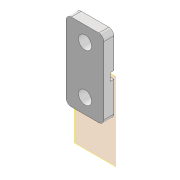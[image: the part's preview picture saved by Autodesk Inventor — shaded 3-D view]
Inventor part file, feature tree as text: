
AUTODESK INVENTOR PART (.ipt)
format: ipt  version: 2020 (Build 240168000, 168)  size: 113,664 bytes
history: native  units: mm
features: other x5, extrude x2, fillet x2, sketch x1
ambient origin geometry x8: Origin, YZ Plane, XZ Plane, XY Plane, X Axis, Y Axis, Z Axis, Center Point
bodies: Body1 (feature_tree)
feature tree (10):
  other  "Sólido1"
  other  "Plano de trabalho1"
  sketch  "Esboço1"  dims[d0=14.0mm d1=14.0mm d2=4.0mm d3=0.0mm d4=1.5mm d5=0.0mm d6=2.0mm d7=5.2mm d8=5.2mm d9=1.5mm]
  extrude  "Extrusão1"  Depth=1.5mm
  extrude  "Extrusão2"  Depth=4.0mm TaperAngle=0.0deg
  fillet  "Arredondamento1"  Radius=1.5mm
  fillet  "Arredondamento2"  Radius=2.0mm
  other  "<userpath>\OneDrive\Área de Trabalho\Calorimetro 2022\Inventor\Montagem_suporte_termopar.iam"
  other  "Montagem_suporte_termopar.iam"
  other  "suporte_termopar_al:1"
